# Revit family: Domotics-SerieCivili-GEWISS-27COMBI_SYSTEM-IP55_RILEVATORI_MOVIMENTO
name_source: partatom
category: Modelli generici
revit_build: Autodesk Revit 2016 (Build: 20161004_0715(x64)
units: mm (PartAtom-declared; Revit-internal decimal feet)

## family parameters
Condiviso = No
Host = Muro
Punto di calcolo locali = No
Può ospitare armatura = No
Quota connettore circolare = Usa diametro
Sempre verticale = Sì
Taglio con vuoti quando caricato = No
Tipo di parte = Normale

## types (1)
- GW27431B - Rivelatore di movimento IR IP55-230V
    Catalogo = DOMOTICS
    Catalogo Serie = 27COMBI
    Classe isolamento = II
    Codice EAN = 8011564825338
    Codice Electrocod = 0143
    Descrizione = RIVELATORE DI MOVIMENTO IR IP55-230V
    Dim. esterne BxHxP (mm) = 72x88x106
    Glow Wire Test = 650°C
    Grado di protezione = IP55
    IDF = f4fab981-b3b7-4adc-a284-171d882b8185
    IDT = 666a0526-0741-48d4-9456-c3f3148265d2
    Immagine tipo = GW27431B.jpg
    Modello = GW27431B
    Norma di riferimento = EN 60669-2-1
    Produttore = GEWISS S.p.A.
    Raggio d'azione = 12m
    Regolazione durata intervento = 5 sec. - 12 min.
    Regolazione soglia crepuscolare = 5 - 1000 lux
    Scheda Tecnica = https://www.gewiss.com
    Temperatura di installazione = -25 +60 °C
    Termopressione con biglia = 70 °C
    URL = https://www.gewiss.com
    Versione file RFA = 18.0

## geometry (parser evidence)
native form markers: Sweep x1
no freeform markers — native parametric forms only
